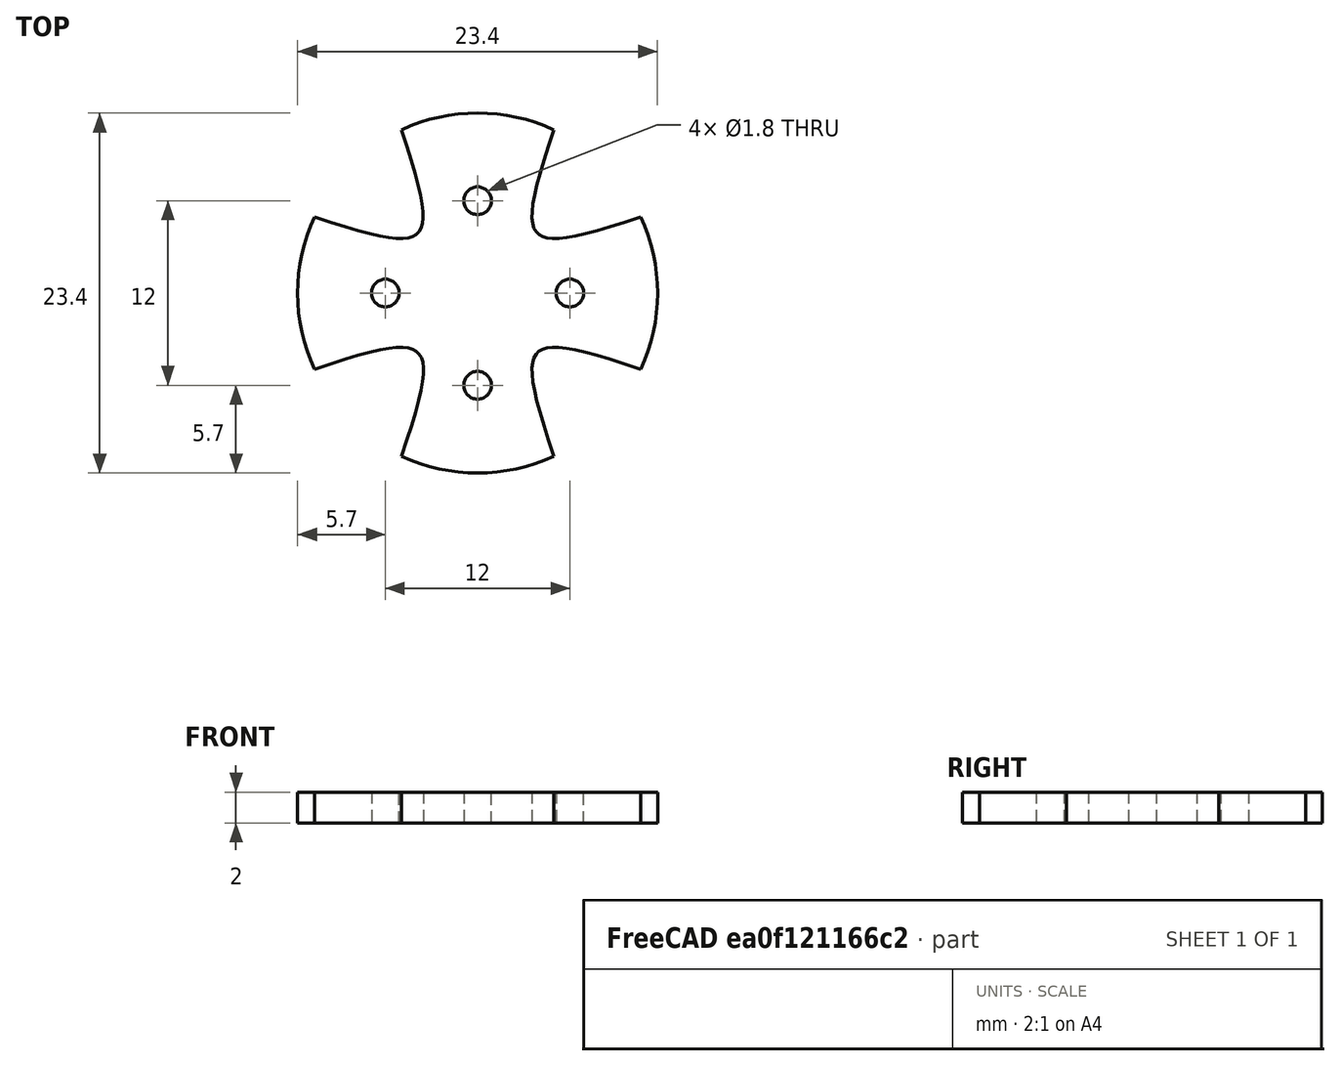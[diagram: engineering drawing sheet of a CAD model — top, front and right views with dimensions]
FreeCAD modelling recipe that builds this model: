
FCSTD DOCUMENT  (FreeCAD 0.19R0.19.2)
Label: boatMoterHolder009
License: All rights reserved
LicenseURL: http://en.wikipedia.org/wiki/All_rights_reserved
objects: Sketcher::SketchObject×2, Part::Extrusion×1
note: 3 computed .brp shape members not serialized (recipe doc carries the construction recipe); baked Part::Feature solids carry a one-line shape summary decoded from their .brp

FEATURE [Sketcher::SketchObject] Sketch
  FullyConstrained = true
  sketch-geometry (44):
    g0: Circle CenterX=-6 CenterY=0 CenterZ=0 NormalX=0 NormalY=0 NormalZ=1 AngleXU=0 Radius=0.9
    g1: Circle CenterX=0 CenterY=6 CenterZ=0 NormalX=0 NormalY=0 NormalZ=1 AngleXU=0 Radius=0.9
    g2: Circle CenterX=6 CenterY=0 CenterZ=0 NormalX=0 NormalY=0 NormalZ=1 AngleXU=0 Radius=0.9
    g3: Circle CenterX=0 CenterY=-6 CenterZ=0 NormalX=0 NormalY=0 NormalZ=1 AngleXU=0 Radius=0.9
    g4-g8: Circle x5 (B-spline internal-alignment scaffolding for g9; pole/knot coordinates omitted)
    g9: BSplineCurve PolesCount=5 KnotsCount=3 Degree=3 IsPeriodic=0
    g10: GeomPoint X=-4.94974 Y=10.6066 Z=0
    g11: GeomPoint X=-3.88908 Y=3.88909 Z=0
    g12: GeomPoint X=-10.6066 Y=4.94975 Z=0
    g13-g17: Circle x5 (B-spline internal-alignment scaffolding for g18; pole/knot coordinates omitted)
    g18: BSplineCurve PolesCount=5 KnotsCount=3 Degree=3 IsPeriodic=0
    g19: GeomPoint X=-10.6066 Y=-4.94974 Z=0
    g20: GeomPoint X=-3.88212 Y=-3.88197 Z=0
    g21: GeomPoint X=-4.94053 Y=-10.6109 Z=0
    g22-g26: Circle x5 (B-spline internal-alignment scaffolding for g27; pole/knot coordinates omitted)
    g27: BSplineCurve PolesCount=5 KnotsCount=3 Degree=3 IsPeriodic=0
    g28: GeomPoint X=4.94975 Y=-10.6066 Z=0
    g29: GeomPoint X=3.8852 Y=-3.88525 Z=0
    g30: GeomPoint X=10.603 Y=-4.95737 Z=0
    g31-g35: Circle x5 (B-spline internal-alignment scaffolding for g36; pole/knot coordinates omitted)
    g36: BSplineCurve PolesCount=5 KnotsCount=3 Degree=3 IsPeriodic=0
    g37: GeomPoint X=10.6066 Y=4.94975 Z=0
    g38: GeomPoint X=3.8891 Y=3.88908 Z=0
    g39: GeomPoint X=4.94975 Y=10.6066 Z=0
    g40: ArcOfCircle CenterX=0 CenterY=0 CenterZ=0 NormalX=0 NormalY=0 NormalZ=1 AngleXU=0 Radius=11.7047 StartAngle=1.13417 EndAngle=2.00742
    g41: ArcOfCircle CenterX=0 CenterY=0 CenterZ=0 NormalX=0 NormalY=0 NormalZ=1 AngleXU=0 Radius=11.7047 StartAngle=5.84584 EndAngle=6.71981
    g42: ArcOfCircle CenterX=0 CenterY=0 CenterZ=0 NormalX=0 NormalY=0 NormalZ=1 AngleXU=0 Radius=11.7047 StartAngle=4.27663 EndAngle=5.14902
    g43: ArcOfCircle CenterX=0 CenterY=0 CenterZ=0 NormalX=0 NormalY=0 NormalZ=1 AngleXU=0 Radius=11.7047 StartAngle=2.70497 EndAngle=3.57822
  constraints (50):
    c: Block(g1)
    c: Block(g2)
    c: Block(g3)
    c: Block(g0)
    c: Weight(g4) = 1
    c: Equal(g4, g5-g8) x4
    c: InternalAlignment(g4-g8 -> g9) x5
    c: InternalAlignment(g10,g9)
    c: InternalAlignment(g11,g9)
    c: InternalAlignment(g12,g9)
    c: Weight(g13) = 1
    c: Equal(g13, g14-g17) x4
    c: InternalAlignment(g13-g17 -> g18) x5
    c: InternalAlignment(g19,g18)
    c: InternalAlignment(g20,g18)
    c: InternalAlignment(g21,g18)
    c: Weight(g22) = 1
    c: Equal(g22,g24)
    c: Equal(g22,g25)
    c: Equal(g22,g26)
    c: InternalAlignment(g22-g26 -> g27) x5
    c: InternalAlignment(g28,g27)
    c: InternalAlignment(g29,g27)
    c: InternalAlignment(g30,g27)
    c: Weight(g31) = 1
    c: Equal(g31, g32-g35) x4
    c: InternalAlignment(g31-g35 -> g36) x5
    c: InternalAlignment(g37,g36)
    c: InternalAlignment(g38,g36)
    c: InternalAlignment(g39,g36)
    c: Coincident(g40,g-1)
    c: Coincident(g40,g9)
    c: Coincident(g40,g36)
    c: Coincident(g41,g40)
    c: Coincident(g41,g36)
    c: Coincident(g41,g27)
    c: Coincident(g42,g40)
    c: Coincident(g42,g27)
    c: Coincident(g42,g18)
    c: Coincident(g43,g40)
    c: Coincident(g43,g18)
    c: Coincident(g43,g9)
    c: Block(g41)
    c: Block(g40)
    c: Block(g43)
    c: Block(g42)
    c: Block(g36)
    c: Block(g9)
    c: Block(g27)
    c: Block(g18)
FEATURE [Part::Extrusion] Extrude
  Base = -> Sketch
  Dir = (0,0,1)
  DirMode = 2
  FaceMakerClass = Part::FaceMakerBullseye
  LengthFwd = 2
  LengthRev = 0
  Solid = true
  Symmetric = false
FEATURE [Sketcher::SketchObject] Sketch001
  FullyConstrained = true
  sketch-geometry (61):
    g0: Circle CenterX=-6 CenterY=0 CenterZ=0 NormalX=0 NormalY=0 NormalZ=1 AngleXU=0 Radius=0.9
    g1: Circle CenterX=0 CenterY=6 CenterZ=0 NormalX=0 NormalY=0 NormalZ=1 AngleXU=0 Radius=0.9
    g2: Circle CenterX=6 CenterY=0 CenterZ=0 NormalX=0 NormalY=0 NormalZ=1 AngleXU=0 Radius=0.9
    g3: Circle CenterX=0 CenterY=-6 CenterZ=0 NormalX=0 NormalY=0 NormalZ=1 AngleXU=0 Radius=0.9
    g4-g8: Circle x5 (B-spline internal-alignment scaffolding for g9; pole/knot coordinates omitted)
    g9: BSplineCurve PolesCount=5 KnotsCount=3 Degree=3 IsPeriodic=0
    g10: GeomPoint X=-4.94974 Y=10.6066 Z=0
    g11: GeomPoint X=-3.88908 Y=3.88909 Z=0
    g12: GeomPoint X=-10.6066 Y=4.94975 Z=0
    g13-g17: Circle x5 (B-spline internal-alignment scaffolding for g18; pole/knot coordinates omitted)
    g18: BSplineCurve PolesCount=5 KnotsCount=3 Degree=3 IsPeriodic=0
    g19: GeomPoint X=-10.6066 Y=-4.94974 Z=0
    g20: GeomPoint X=-3.88212 Y=-3.88197 Z=0
    g21: GeomPoint X=-4.94053 Y=-10.6109 Z=0
    g22-g26: Circle x5 (B-spline internal-alignment scaffolding for g27; pole/knot coordinates omitted)
    g27: BSplineCurve PolesCount=5 KnotsCount=3 Degree=3 IsPeriodic=0
    g28: GeomPoint X=4.94975 Y=-10.6066 Z=0
    g29: GeomPoint X=3.8852 Y=-3.88525 Z=0
    g30: GeomPoint X=10.603 Y=-4.95737 Z=0
    g31-g35: Circle x5 (B-spline internal-alignment scaffolding for g36; pole/knot coordinates omitted)
    g36: BSplineCurve PolesCount=5 KnotsCount=3 Degree=3 IsPeriodic=0
    g37: GeomPoint X=10.6066 Y=4.94975 Z=0
    g38: GeomPoint X=3.8891 Y=3.88908 Z=0
    g39: GeomPoint X=4.94975 Y=10.6066 Z=0
    g40: ArcOfCircle CenterX=0 CenterY=0 CenterZ=0 NormalX=0 NormalY=0 NormalZ=1 AngleXU=0 Radius=11.7047 StartAngle=1.13417 EndAngle=1.50239
    g41: ArcOfCircle CenterX=0 CenterY=0 CenterZ=0 NormalX=0 NormalY=0 NormalZ=1 AngleXU=0 Radius=11.7047 StartAngle=5.84584 EndAngle=6.21478
    g42: ArcOfCircle CenterX=0 CenterY=0 CenterZ=0 NormalX=0 NormalY=0 NormalZ=1 AngleXU=0 Radius=11.7047 StartAngle=4.27663 EndAngle=4.64399
    g43: ArcOfCircle CenterX=0 CenterY=0 CenterZ=0 NormalX=0 NormalY=0 NormalZ=1 AngleXU=0 Radius=11.7047 StartAngle=2.70497 EndAngle=3.07319
    g44: LineSegment StartX=22.4 StartY=-0.8 StartZ=0 EndX=11.6773 EndY=-0.8 EndZ=0
    g45: LineSegment StartX=22.4 StartY=0.8 StartZ=0 EndX=11.6773 EndY=0.8 EndZ=0
    g46: LineSegment StartX=0.8 StartY=22.4 StartZ=0 EndX=0.8 EndY=11.6773 EndZ=0
    g47: LineSegment StartX=-0.8 StartY=22.4 StartZ=0 EndX=-0.8 EndY=11.6773 EndZ=0
    g48: LineSegment StartX=-22.4 StartY=0.8 StartZ=0 EndX=-11.6773 EndY=0.8 EndZ=0
    g49: LineSegment StartX=-22.4 StartY=-0.8 StartZ=0 EndX=-11.6773 EndY=-0.8 EndZ=0
    g50: LineSegment StartX=-22.4 StartY=0.8 StartZ=0 EndX=-22.4 EndY=-0.8 EndZ=0
    g51: ArcOfCircle CenterX=0 CenterY=0 CenterZ=0 NormalX=0 NormalY=0 NormalZ=1 AngleXU=0 Radius=11.7047 StartAngle=3.20999 EndAngle=3.57822
    g52: ArcOfCircle CenterX=0 CenterY=0 CenterZ=0 NormalX=0 NormalY=0 NormalZ=1 AngleXU=0 Radius=11.7047 StartAngle=1.6392 EndAngle=2.00742
    g53: ArcOfCircle CenterX=0 CenterY=0 CenterZ=0 NormalX=0 NormalY=0 NormalZ=1 AngleXU=0 Radius=11.7047 StartAngle=0.0684019 EndAngle=0.436627
    g54: LineSegment StartX=-0.8 StartY=22.4 StartZ=0 EndX=0.8 EndY=22.4 EndZ=0
    g55: LineSegment StartX=22.4 StartY=-0.8 StartZ=0 EndX=22.4 EndY=0.8 EndZ=0
    g56: LineSegment StartX=0 StartY=0 StartZ=0 EndX=0 EndY=-6 EndZ=0
    g57: LineSegment StartX=0.8 StartY=-22.4 StartZ=0 EndX=0.8 EndY=-11.6773 EndZ=0
    g58: LineSegment StartX=-0.8 StartY=-22.4 StartZ=0 EndX=-0.8 EndY=-11.6773 EndZ=0
    g59: LineSegment StartX=-0.8 StartY=-22.4 StartZ=0 EndX=0.8 EndY=-22.4 EndZ=0
    g60: ArcOfCircle CenterX=0 CenterY=0 CenterZ=0 NormalX=0 NormalY=0 NormalZ=1 AngleXU=0 Radius=11.7047 StartAngle=4.78079 EndAngle=5.14902
  constraints (100):
    c: Block(g1)
    c: Block(g2)
    c: Block(g3)
    c: Block(g0)
    c: Weight(g4) = 1
    c: Equal(g4, g5-g8) x4
    c: InternalAlignment(g4-g8 -> g9) x5
    c: InternalAlignment(g10,g9)
    c: InternalAlignment(g11,g9)
    c: InternalAlignment(g12,g9)
    c: Weight(g13) = 1
    c: Equal(g13, g14-g17) x4
    c: InternalAlignment(g13-g17 -> g18) x5
    c: InternalAlignment(g19,g18)
    c: InternalAlignment(g20,g18)
    c: InternalAlignment(g21,g18)
    c: Weight(g22) = 1
    c: Equal(g22,g24)
    c: Equal(g22,g25)
    c: Equal(g22,g26)
    c: InternalAlignment(g22-g26 -> g27) x5
    c: InternalAlignment(g28,g27)
    c: InternalAlignment(g29,g27)
    c: InternalAlignment(g30,g27)
    c: Weight(g31) = 1
    c: Equal(g31, g32-g35) x4
    c: InternalAlignment(g31-g35 -> g36) x5
    c: InternalAlignment(g37,g36)
    c: InternalAlignment(g38,g36)
    c: InternalAlignment(g39,g36)
    c: Coincident(g40,g-1)
    c: Coincident(g52,g9)
    c: Coincident(g40,g36)
    c: Coincident(g41,g40)
    c: Coincident(g53,g36)
    c: Coincident(g41,g27)
    c: Coincident(g42,g40)
    c: Coincident(g60,g27)
    c: Coincident(g42,g18)
    c: Coincident(g43,g40)
    c: Coincident(g51,g18)
    c: Coincident(g43,g9)
    c: Block(g41)
    c: Block(g40)
    c: Block(g43)
    c: Block(g42)
    c: Block(g36)
    c: Block(g9)
    c: Block(g27)
    c: Block(g18)
    c: Horizontal(g44)
    c: Horizontal(g45)
    c: Vertical(g46)
    c: Vertical(g47)
    c: Horizontal(g48)
    c: Horizontal(g49)
    c: Block(g49)
    c: Block(g48)
    c: Block(g47)
    c: Block(g46)
    c: Block(g45)
    c: Block(g44)
    c: Coincident(g50,g48)
    c: Coincident(g50,g49)
    c: Vertical(g50)
    c: Distance(g50) = 1.6
    c: Equal(g43,g51)
    c: Coincident(g43,g48)
    c: Coincident(g51,g49)
    c: Coincident(g43,g51)
    c: Equal(g40,g52)
    c: Coincident(g40,g46)
    c: Coincident(g52,g47)
    c: Coincident(g40,g52)
    c: Equal(g41,g53)
    c: Coincident(g41,g44)
    c: PointOnObject(g53,g45)
    c: Coincident(g41,g53)
    c: Coincident(g54,g47)
    c: Coincident(g54,g46)
    c: Horizontal(g54)
    c: Distance(g54) = 1.6
    c: Coincident(g55,g44)
    c: Coincident(g55,g45)
    c: Vertical(g55)
    c: Distance(g55) = 1.6
    c: Coincident(g56,g40)
    c: Coincident(g56,g3)
    c: Vertical(g56)
    c: Vertical(g57)
    c: Vertical(g58)
    c: Block(g57)
    c: Block(g58)
    c: Coincident(g59,g58)
    c: Coincident(g59,g57)
    c: Horizontal(g59)
    c: Equal(g42,g60)
    c: Coincident(g42,g58)
    c: Coincident(g60,g57)
    c: Coincident(g42,g60)
